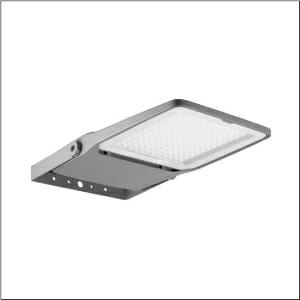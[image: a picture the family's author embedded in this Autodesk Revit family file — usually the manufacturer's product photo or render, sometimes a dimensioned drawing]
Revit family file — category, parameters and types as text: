
# Revit family: floodlight_fl_20_midi___pl52_5xa7682d3d2ac_85b5
name_source: partatom
category: Lighting Fixtures
units: mm (PartAtom-declared; Revit-internal decimal feet)

## family parameters
Cut with Voids When Loaded = No
Host = Face
Light Source = No
Part Type = Normal
Room Calculation Point = No
Round Connector Dimension = Use Diameter
Shared = No

## types (1)
- --- (1 x LED 5000K / CRI = 70 (unbekannt), 18250 lm, 5000K)
    Apparent Load = 142 VA
    CIE Flux Codes = 27 59 98 100 100
    Color Rendering = 70
    Color Temperature = 5000K
    Default Elevation = 1800 mm
    Description = Floodlight FL 20 midi, floodlight, primary light control with lens, of plastic, primary optical cover: protective disc, of toughened safety glass, transparent, light distribution: PL52, light emission: direct distribution, primary light characteristic: asymmetric, installation type: surface-mounted, LED, High Power LED, rated luminous flux: 18.250lm, luminous efficacy: 129lm/W, light colour: 750, colour temperature: 5000K, control gear: ECG Plus, control: flexible luminous flux parameterisation, time-dependent luminous flux control, digital communication interface, power reduction, overheat protection, electronic power reduction, with terminal, 5-pole, max. 2.5mm², mains connection: 220..240V, AC, 50/60Hz, rated input power: 142W, LED unit, of diecast aluminium, powder-coated, Siteco® metallic grey (DB 702S), corrosivity category C5 mid according to DIN EN ISO 12944, incl. 1x M20 cable gland for cable Ø 6.5..12mm, length: 731mm, width: 450mm, height: 76mm, housing frame, of diecast aluminium, powder-coated, Siteco® metallic grey (DB 702S), wall fastening, of steel, powder-coated, Siteco® metallic grey (DB 702S), DALI, protection rating (complete): IP66, insulation class (complete): insulation class II (safety insulation), certification: CE, ENEC, VDE, protection symbol: D, permissible operating ambient temperature: -40..+40°C, permissible operating ambient temperature for outdoor applications: -40..+50°C, standard: DIN EN 12944, packaging unit: 1 piece

Light Distribution: PL52
    Height = 76 mm
    Lamp = 1 x LED 5000K / CRI >= 70 (unbekannt)
    Lamp Light Flux = 18250 lm
    Lamp count = 1
    Length = 731 mm
    Luminous efficacy = 129 lm/W
    Manufacturer = Siteco
    ModVariant = No
    Model = 5XA7682D3D2AC
    Mounting Place = Wall
    Mounting Type = Surface mounted
    Number of Poles = 1
    OnlyDefault = Yes
    Power Factor = 1
    Product Name = Floodlight FL 20 midi | PL52
    Product group = floodlight | wall mounted
    ProductGroupID = 2001
    Protection Class = Protection class II
    Protection Degree = IP 66
    RLX_Detail_Level = 1
    RLX_Emergency_Light_Flux = 0 lm
    RLX_Emergency_Type = 0
    RLX_Emergency_Type_DB = No
    RlxData = <blob elided: 92457 chars, md5=9d78458a>
    Socket = socket
    Standby Power = 0 W
    System Light Flux = 18250 lm
    System Power = 142 W
    Type Comments = factory setting: luminous flux: 100 % | dim-lin: 254 | 489 mA
    Type Image = l_1005944.jpg
    URL = http://relux.com
    VarID = @adj_147787
    Voltage = 0 V
    Weight = 0.00 kg
    Width = 450 mm

## geometry (parser evidence)
native form markers: Blend x4, Sweep x13
no freeform markers — native parametric forms only
